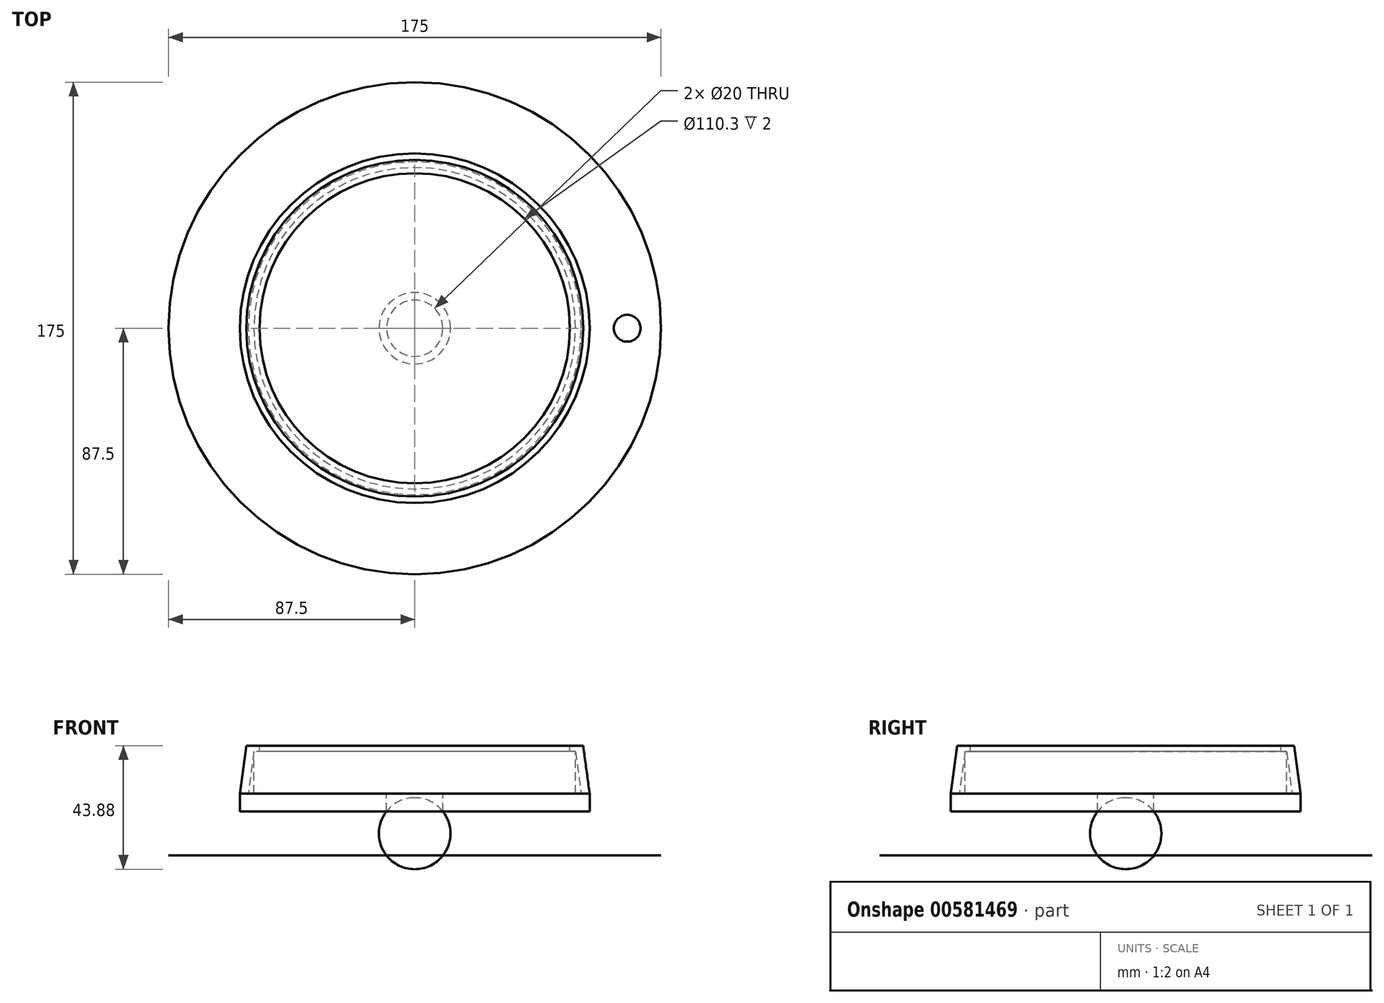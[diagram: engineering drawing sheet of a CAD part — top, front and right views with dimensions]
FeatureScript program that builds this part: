
annotation { "Feature Type Name" : "Feature", "Feature Type Description" : "" }
export const myFeature = defineFeature(function(context is Context, id is Id, definition is map)
    precondition{}
    {
        {
            var Q0;
            Q0=qCreatedBy(makeId("Top.planeOp"),FACE);
            var sketch = newSketch(context, id + "F0", { "sketchPlane" : qUnion([Q0])});
            skCircle(sketch, "E0", {"center": v(0, 0) * mm, "radius": 87.5 * mm});
            skCircle(sketch, "E1", {"center": v(75.5, 0) * mm, "radius": 4.76 * mm});
            skCircle(sketch, "E2", {"center": v(0, 0) * mm, "radius": 57.15 * mm, "construction": true});
            skLineSegment(sketch, "E3", {"start": v(57.15, 0) * mm, "end": v(87.5, 0) * mm, "construction": true});
            skCircle(sketch, "E4", {"center": v(0, 0) * mm, "radius": 10 * mm});
            skPoint(sketch, "E5", {"position": v(-10, 0) * mm});
            skPoint(sketch, "E6", {"position": v(10, 0) * mm});
            skSolve(sketch);
        }
        {
            var Q0;
            Q0 = qSketchRegion(id + "F0", true);
            var Q1;
            Q1=makeQuery(id+"F0.imprint","IMPRINT",FACE,{"disambiguationData":[TD([[makeQuery(id+"F0.imprint","IMPRINT",EDGE,{"derivedFrom":sQuery(id+"F0.wireOp",EDGE,"NLsv2Z5s-ldcv-p21d-6igh-SqaTtoUgnMiu")}),1.0]])]});
            var Q2;
            Q2=makeQuery(id+"F0.imprint","IMPRINT",FACE,{"disambiguationData":[TD([[makeQuery(id+"F0.imprint","IMPRINT",EDGE,{"derivedFrom":sQuery(id+"F0.wireOp",EDGE,"E1")}),1.0]])]});
            var Q3;
            Q3=makeQuery(id+"F0.imprint","IMPRINT",FACE,{"disambiguationData":[TD([[makeQuery(id+"F0.imprint","IMPRINT",EDGE,{"derivedFrom":sQuery(id+"F0.wireOp",EDGE,"E4")}),-1.0]])]});
            extrude(context, id + "F1", {"entities" : qUnion([Q0, Q1, Q2, Q3]), "oppositeDirection" : true, "depth" : 1 / 101.6 * mm, "offsetDistance" : 25 * mm});
        }
        {
            var Q0;
            Q0=makeQuery(id+"F0.imprint","IMPRINT",FACE,{"disambiguationData":[TD([[makeQuery(id+"F0.imprint","IMPRINT",EDGE,{"derivedFrom":sQuery(id+"F0.wireOp",EDGE,"E1")}),1.0]])]});
            var Q1;
            Q1=makeQuery(id+"F1.opExtrude","CAP_FACE",FACE,{"disambiguationData":[OSD([sQuery(id+"F0.wireOp",EDGE,"E0")])],"isStart":false});
            extrude(context, id + "F2", {"entities" : qUnion([Q0]), "operationType" : NewBodyOperationType.REMOVE, "endBound" : BoundingType.UP_TO_SURFACE, "oppositeDirection" : true, "depth" : 25 * mm, "endBoundEntityFace" : qUnion([Q1]), "offsetDistance" : 25 * mm});
        }
        {
            var Q0;
            Q0=qCreatedBy(makeId("Front.planeOp"),FACE);
            var sketch = newSketch(context, id + "F3", { "sketchPlane" : qUnion([Q0])});
            skCircle(sketch, "E7", {"center": v(0, 7.83) * mm, "radius": 12.7 * mm});
            skPoint(sketch, "E8.0", {"position": v(10, 0) * mm});
            skPoint(sketch, "E8.1", {"position": v(-10, 0) * mm});
            skLineSegment(sketch, "E9", {"start": v(0, 20.53) * mm, "end": v(0, -4.87) * mm});
            skLineSegment(sketch, "E10", {"start": v(-10, 0) * mm, "end": v(-10, 15.66) * mm, "construction": true});
            skLineSegment(sketch, "E11", {"start": v(10, 0) * mm, "end": v(10, 15.66) * mm, "construction": true});
            skLineSegment(sketch, "E12", {"start": v(10, 15.66) * mm, "end": v(10, 22) * mm});
            skLineSegment(sketch, "E13", {"start": v(10, 22) * mm, "end": v(62.15, 22) * mm});
            skLineSegment(sketch, "E14", {"start": v(62.15, 22) * mm, "end": v(62.15, 15.66) * mm});
            skLineSegment(sketch, "E15", {"start": v(62.15, 15.66) * mm, "end": v(10, 15.66) * mm});
            skLineSegment(sketch, "E16", {"start": v(0, 22) * mm, "end": v(57.15, 22) * mm});
            skLineSegment(sketch, "E17", {"start": v(57.15, 22) * mm, "end": v(57.15, 37) * mm});
            skLineSegment(sketch, "E18", {"start": v(57.15, 37) * mm, "end": v(0, 37) * mm});
            skLineSegment(sketch, "E19", {"start": v(0, 37) * mm, "end": v(0, 22) * mm});
            skLineSegment(sketch, "E20", {"start": v(55.15, 37) * mm, "end": v(55.15, 39) * mm});
            skLineSegment(sketch, "E21", {"start": v(55.15, 39) * mm, "end": v(59.88, 39) * mm});
            skLineSegment(sketch, "E22", {"start": v(59.88, 39) * mm, "end": v(62.15, 22) * mm});
            skLineSegment(sketch, "E23", {"start": v(62.15, 22) * mm, "end": v(59.15, 22) * mm});
            skLineSegment(sketch, "E24", {"start": v(59.15, 22) * mm, "end": v(57.15, 37) * mm});
            skLineSegment(sketch, "E25", {"start": v(57.15, 22) * mm, "end": v(59.15, 22) * mm, "construction": true});
            skSolve(sketch);
        }
        {
            var Q0;
            {var subQ0=sQuery(id+"F3.wireOp",EDGE,"E9");Q0=makeQuery(id+"F3.imprint","IMPRINT",FACE,{"disambiguationData":[TD([[makeQuery(id+"F3.imprint","IMPRINT",EDGE,{"derivedFrom":subQ0}),-1.0]])]});}
            var Q1;
            Q1=sQuery(id+"F3.wireOp",EDGE,"E9");
            revolve(context, id + "F4", {"entities" : qUnion([Q0]), "axis" : qUnion([Q1]), "revolveType" : RevolveType.FULL});
        }
        {
            var Q0;
            {var subQ1=sQuery(id+"F3.wireOp",EDGE,"E17");Q0=makeQuery(id+"F3.imprint","IMPRINT",FACE,{"disambiguationData":[TD([[makeQuery(id+"F3.imprint","IMPRINT",EDGE,{"derivedFrom":subQ1}),1.0]])]});}
            var Q1;
            Q1=sQuery(id+"F3.wireOp",EDGE,"E19");
            revolve(context, id + "F5", {"entities" : qUnion([Q0]), "axis" : qUnion([Q1]), "revolveType" : RevolveType.FULL});
        }
        {
            var Q0;
            {var subQ1=sQuery(id+"F3.wireOp",EDGE,"E12");Q0=makeQuery(id+"F3.imprint","IMPRINT",FACE,{"disambiguationData":[TD([[makeQuery(id+"F3.imprint","IMPRINT",EDGE,{"derivedFrom":subQ1}),-1.0]])]});}
            var Q1;
            Q1=sQuery(id+"F3.wireOp",EDGE,"E9");
            revolve(context, id + "F6", {"entities" : qUnion([Q0]), "axis" : qUnion([Q1]), "revolveType" : RevolveType.FULL});
        }
        {
            var Q0;
            {var subQ0=sQuery(id+"F3.wireOp",EDGE,"E20");Q0=makeQuery(id+"F3.imprint","IMPRINT",FACE,{"disambiguationData":[TD([[makeQuery(id+"F3.imprint","IMPRINT",EDGE,{"derivedFrom":subQ0}),-1.0]])]});}
            var Q1;
            Q1=sQuery(id+"F3.wireOp",EDGE,"E19");
            revolve(context, id + "F7", {"entities" : qUnion([Q0]), "axis" : qUnion([Q1]), "revolveType" : RevolveType.FULL});
        }
    });
